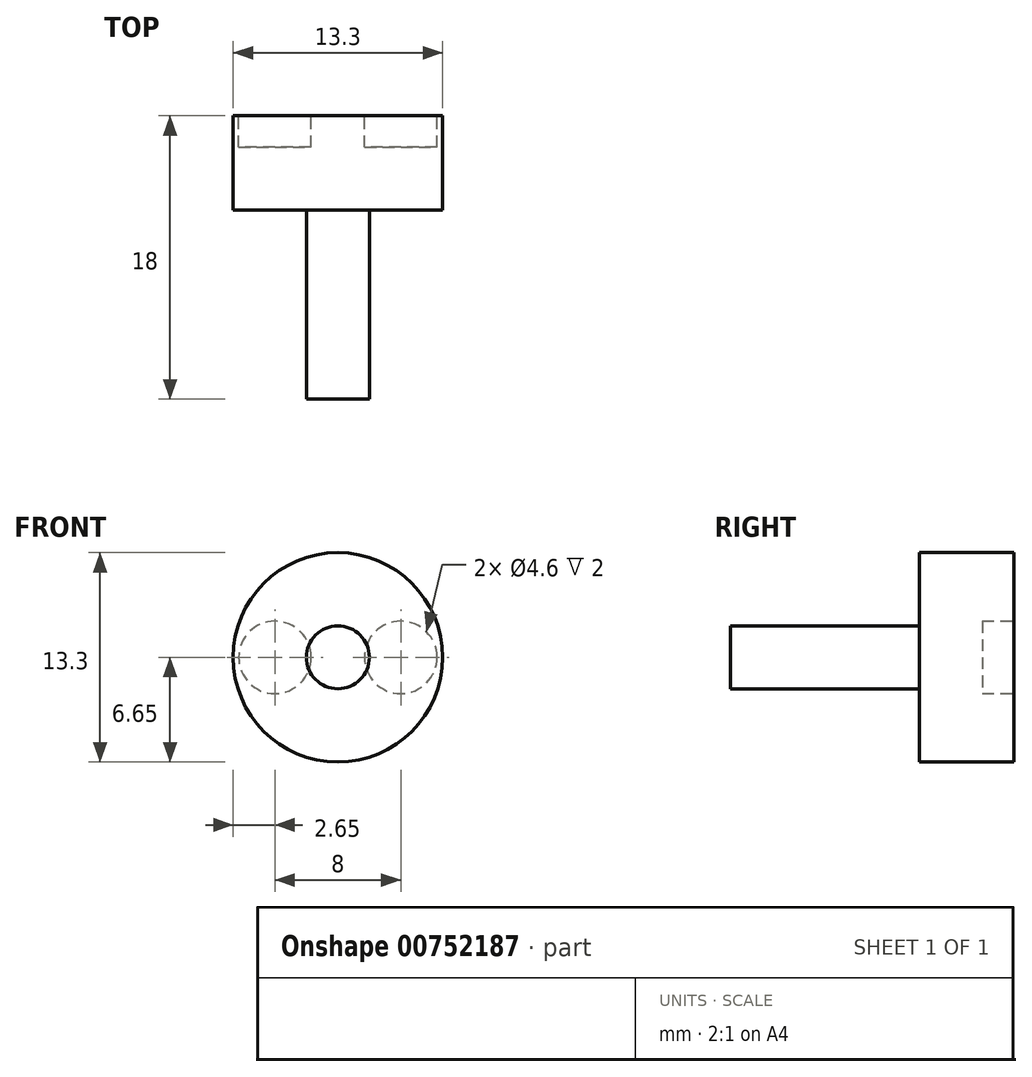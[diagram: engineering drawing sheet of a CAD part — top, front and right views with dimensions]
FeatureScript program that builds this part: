
annotation { "Feature Type Name" : "Feature", "Feature Type Description" : "" }
export const myFeature = defineFeature(function(context is Context, id is Id, definition is map)
    precondition{}
    {
        {
            var Q0;
            Q0=qCreatedBy(makeId("Front.planeOp"),FACE);
            var sketch = newSketch(context, id + "F0", { "sketchPlane" : qUnion([Q0])});
            skCircle(sketch, "E0", {"center": v(0, 0) * mm, "radius": 6.65 * mm});
            skSolve(sketch);
        }
        {
            var Q0;
            Q0=qSketchRegion(id+"F0",true);
            extrude(context, id + "F1", {"entities" : qUnion([Q0]), "depth" : 6 * mm, "offsetDistance" : 25 * mm});
        }
        {
            var Q0;
            Q0=makeQuery(id+"F1.opExtrude","CAP_FACE",FACE,{"disambiguationData":[OSD([sQuery(id+"F0.wireOp",EDGE,"E0")])],"isStart":false});
            var sketch = newSketch(context, id + "F2", { "sketchPlane" : qUnion([Q0])});
            skCircle(sketch, "E1", {"center": v(0, 0) * mm, "radius": 2 * mm});
            skSolve(sketch);
        }
        {
            var Q0;
            Q0=qSketchRegion(id+"F2",true);
            extrude(context, id + "F3", {"entities" : qUnion([Q0]), "operationType" : NewBodyOperationType.ADD, "depth" : 12 * mm, "offsetDistance" : 25 * mm});
        }
        {
            var Q0;
            Q0=makeQuery(id+"F1.opExtrude","CAP_FACE",FACE,{"disambiguationData":[OSD([sQuery(id+"F0.wireOp",EDGE,"E0")])],"isStart":true});
            var sketch = newSketch(context, id + "F4", { "sketchPlane" : qUnion([Q0])});
            skCircle(sketch, "E2", {"center": v(-4, 0) * mm, "radius": 2.3 * mm});
            skCircle(sketch, "E3", {"center": v(4, 0) * mm, "radius": 2.3 * mm});
            skSolve(sketch);
        }
        {
            var Q0;
            Q0=qSketchRegion(id+"F4",true);
            extrude(context, id + "F5", {"entities" : qUnion([Q0]), "operationType" : NewBodyOperationType.REMOVE, "oppositeDirection" : true, "depth" : 2 * mm, "offsetDistance" : 25 * mm});
        }
    });
